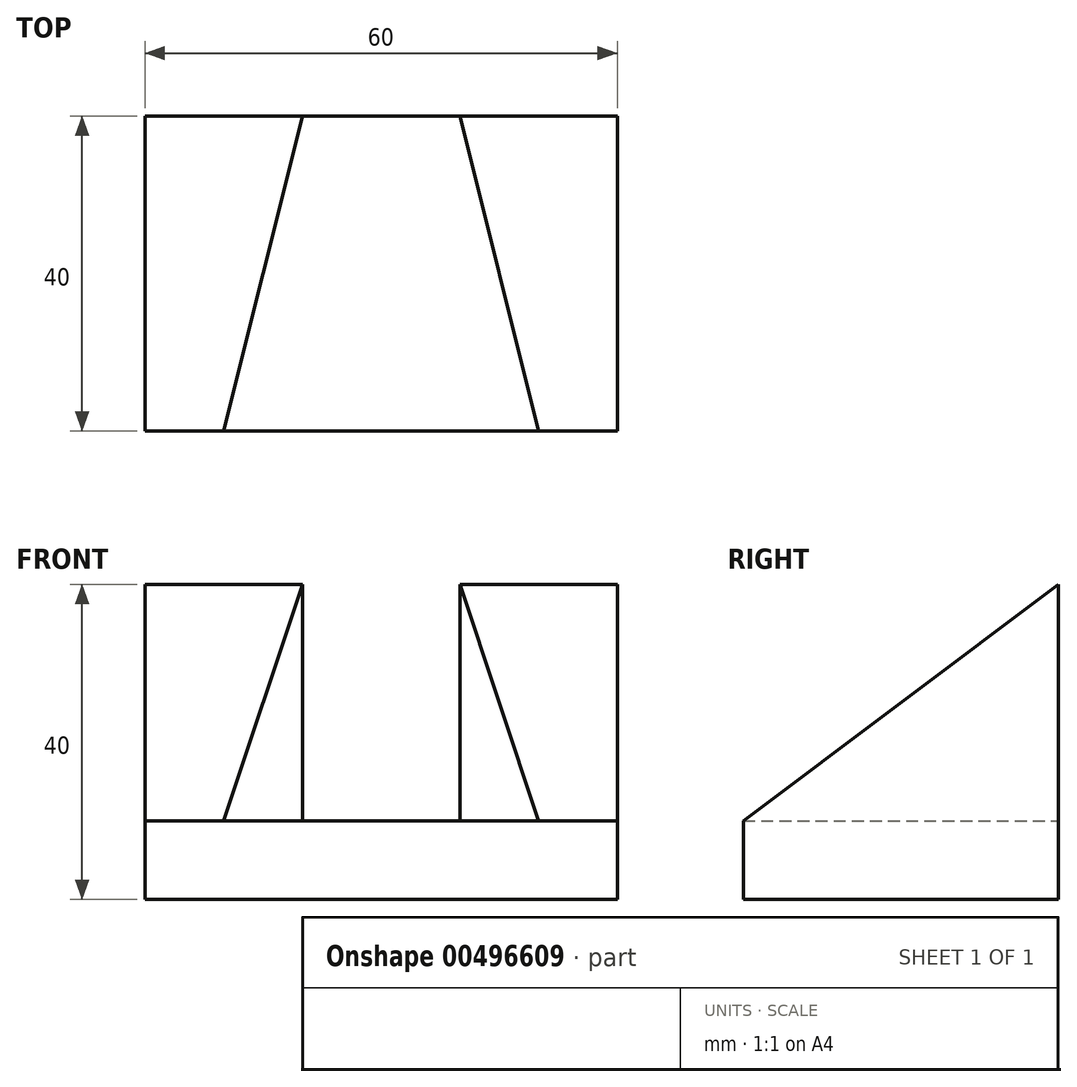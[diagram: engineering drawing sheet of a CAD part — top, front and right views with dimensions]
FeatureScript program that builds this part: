
annotation { "Feature Type Name" : "Feature", "Feature Type Description" : "" }
export const myFeature = defineFeature(function(context is Context, id is Id, definition is map)
    precondition{}
    {
        {
            var Q0;
            Q0=qCreatedBy(makeId("Top.planeOp"),FACE);
            var sketch = newSketch(context, id + "F0", { "sketchPlane" : qUnion([Q0])});
            skLineSegment(sketch, "E0", {"start": v(0, 0) * mm, "end": v(60, 0) * mm});
            skLineSegment(sketch, "E1", {"start": v(60, 0) * mm, "end": v(60, 40) * mm});
            skLineSegment(sketch, "E2", {"start": v(60, 40) * mm, "end": v(0, 40) * mm});
            skLineSegment(sketch, "E3", {"start": v(0, 40) * mm, "end": v(0, 0) * mm});
            skSolve(sketch);
        }
        {
            var Q0;
            Q0 = qSketchRegion(id + "F0", true);
            extrude(context, id + "F1", {"entities" : qUnion([Q0]), "depth" : 10 * mm});
        }
        {
            var Q0;
            Q0=makeQuery(id+"F1.opExtrude","CAP_FACE",FACE,{"disambiguationData":[OSD([sQuery(id+"F0.wireOp",EDGE,"E0"),sQuery(id+"F0.wireOp",EDGE,"E1"),sQuery(id+"F0.wireOp",EDGE,"E2"),sQuery(id+"F0.wireOp",EDGE,"E3")])],"isStart":false});
            var sketch = newSketch(context, id + "F2", { "sketchPlane" : qUnion([Q0])});
            skLineSegment(sketch, "E4", {"start": v(0, 40) * mm, "end": v(0, 0) * mm});
            skLineSegment(sketch, "E5", {"start": v(0, 0) * mm, "end": v(10, 0) * mm});
            skLineSegment(sketch, "E6", {"start": v(0, 40) * mm, "end": v(20, 40) * mm});
            skLineSegment(sketch, "E7", {"start": v(20, 40) * mm, "end": v(10, 0) * mm});
            skLineSegment(sketch, "E8", {"start": v(60, 40) * mm, "end": v(40, 40) * mm});
            skLineSegment(sketch, "E9", {"start": v(60, 40) * mm, "end": v(60, 0) * mm});
            skLineSegment(sketch, "E10", {"start": v(60, 0) * mm, "end": v(50, 0) * mm});
            skLineSegment(sketch, "E11", {"start": v(50, 0) * mm, "end": v(40, 40) * mm});
            skSolve(sketch);
        }
        {
            var Q0;
            Q0 = qSketchRegion(id + "F2", true);
            extrude(context, id + "F3", {"entities" : qUnion([Q0]), "operationType" : NewBodyOperationType.ADD, "depth" : 30 * mm});
        }
        {
            var Q0;
            Q0=makeQuery(id+"F3.opExtrude","CAP_EDGE",EDGE,{"disambiguationData":[OSD([sQuery(id+"F2.wireOp",EDGE,"E10")])],"isStart":false});
            var Q1;
            Q1=makeQuery(id+"F3.opExtrude","CAP_EDGE",EDGE,{"disambiguationData":[OSD([sQuery(id+"F2.wireOp",EDGE,"E5")])],"isStart":false});
            chamfer(context, id + "F4", {"entities" : qUnion([Q0, Q1]), "chamferType" : ChamferType.TWO_OFFSETS, "width1" : 40 * mm, "oppositeDirection" : false, "width2" : 30 * mm, "tangentPropagation" : true});
        }
    });
